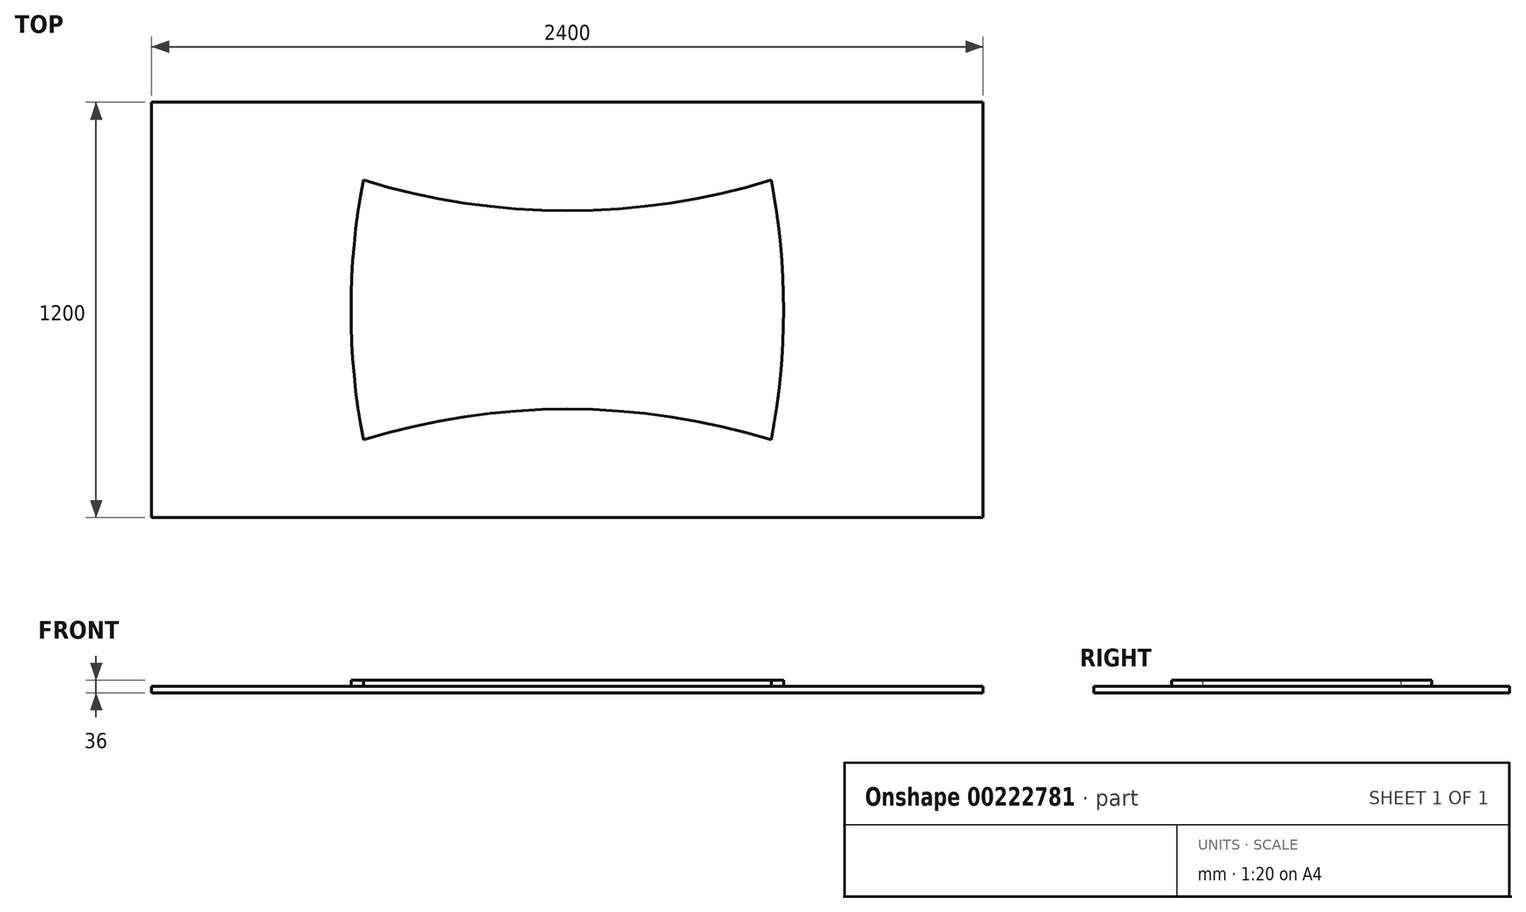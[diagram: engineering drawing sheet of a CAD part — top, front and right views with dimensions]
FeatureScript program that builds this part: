
annotation { "Feature Type Name" : "Feature", "Feature Type Description" : "" }
export const myFeature = defineFeature(function(context is Context, id is Id, definition is map)
    precondition{}
    {
        {
            var Q0;
            Q0=qCreatedBy(makeId("Top.planeOp"),FACE);
            var sketch = newSketch(context, id + "F0", { "sketchPlane" : qUnion([Q0])});
            skLineSegment(sketch, "E0.bottom", {"start": v(-590, 290) * mm, "end": v(590, 290) * mm, "construction": true});
            skLineSegment(sketch, "E0.top", {"start": v(-590, -290) * mm, "end": v(590, -290) * mm, "construction": true});
            skLineSegment(sketch, "E0.left", {"start": v(-590, 290) * mm, "end": v(-590, -290) * mm, "construction": true});
            skLineSegment(sketch, "E0.right", {"start": v(590, 290) * mm, "end": v(590, -290) * mm, "construction": true});
            skPoint(sketch, "E0.middle", {"position": v(0, 0) * mm});
            skLineSegment(sketch, "E1", {"start": v(0, 254.16) * mm, "end": v(0, -247.53) * mm, "construction": true});
            skLineSegment(sketch, "E2", {"start": v(-547.35, 0) * mm, "end": v(503.45, 0) * mm, "construction": true});
            skArc(sketch, "E3", {"start": v(-588.85, 375.2) * mm, "mid": v(-615.47, 188.44) * mm, "end": v(-624.36, 0) * mm});
            skArc(sketch, "E4.MirrorCS", {"start": v(-588.85, -375.2) * mm, "mid": v(-615.47, -188.44) * mm, "end": v(-624.36, 0) * mm});
            skArc(sketch, "E5.MirrorCS", {"start": v(588.85, -375.2) * mm, "mid": v(615.47, -188.44) * mm, "end": v(624.36, 0) * mm});
            skArc(sketch, "E6.MirrorCS", {"start": v(588.85, 375.2) * mm, "mid": v(615.47, 188.44) * mm, "end": v(624.36, 0) * mm});
            skArc(sketch, "E7", {"start": v(-588.85, 375.2) * mm, "mid": v(0, 286.55) * mm, "end": v(588.85, 375.2) * mm});
            skArc(sketch, "E8.MirrorCS", {"start": v(-588.85, -375.2) * mm, "mid": v(0, -286.55) * mm, "end": v(588.85, -375.2) * mm});
            skPoint(sketch, "E9", {"position": v(0, -286.55) * mm});
            skSolve(sketch);
        }
        {
            var Q0;
            Q0 = qSketchRegion(id + "F0", true);
            extrude(context, id + "F1", {"entities" : qUnion([Q0]), "depth" : 18 * mm});
        }
        {
            var Q0;
            Q0=qCreatedBy(makeId("Top.planeOp"),FACE);
            var sketch = newSketch(context, id + "F2", { "sketchPlane" : qUnion([Q0])});
            skLineSegment(sketch, "E10.bottom", {"start": v(-1200, 600) * mm, "end": v(1200, 600) * mm});
            skLineSegment(sketch, "E10.top", {"start": v(-1200, -600) * mm, "end": v(1200, -600) * mm});
            skLineSegment(sketch, "E10.left", {"start": v(-1200, 600) * mm, "end": v(-1200, -600) * mm});
            skLineSegment(sketch, "E10.right", {"start": v(1200, 600) * mm, "end": v(1200, -600) * mm});
            skPoint(sketch, "E10.middle", {"position": v(0, 0) * mm});
            skSolve(sketch);
        }
        {
            var Q0;
            Q0 = qSketchRegion(id + "F2", true);
            extrude(context, id + "F3", {"entities" : qUnion([Q0]), "oppositeDirection" : true, "depth" : 18 * mm});
        }
    });
